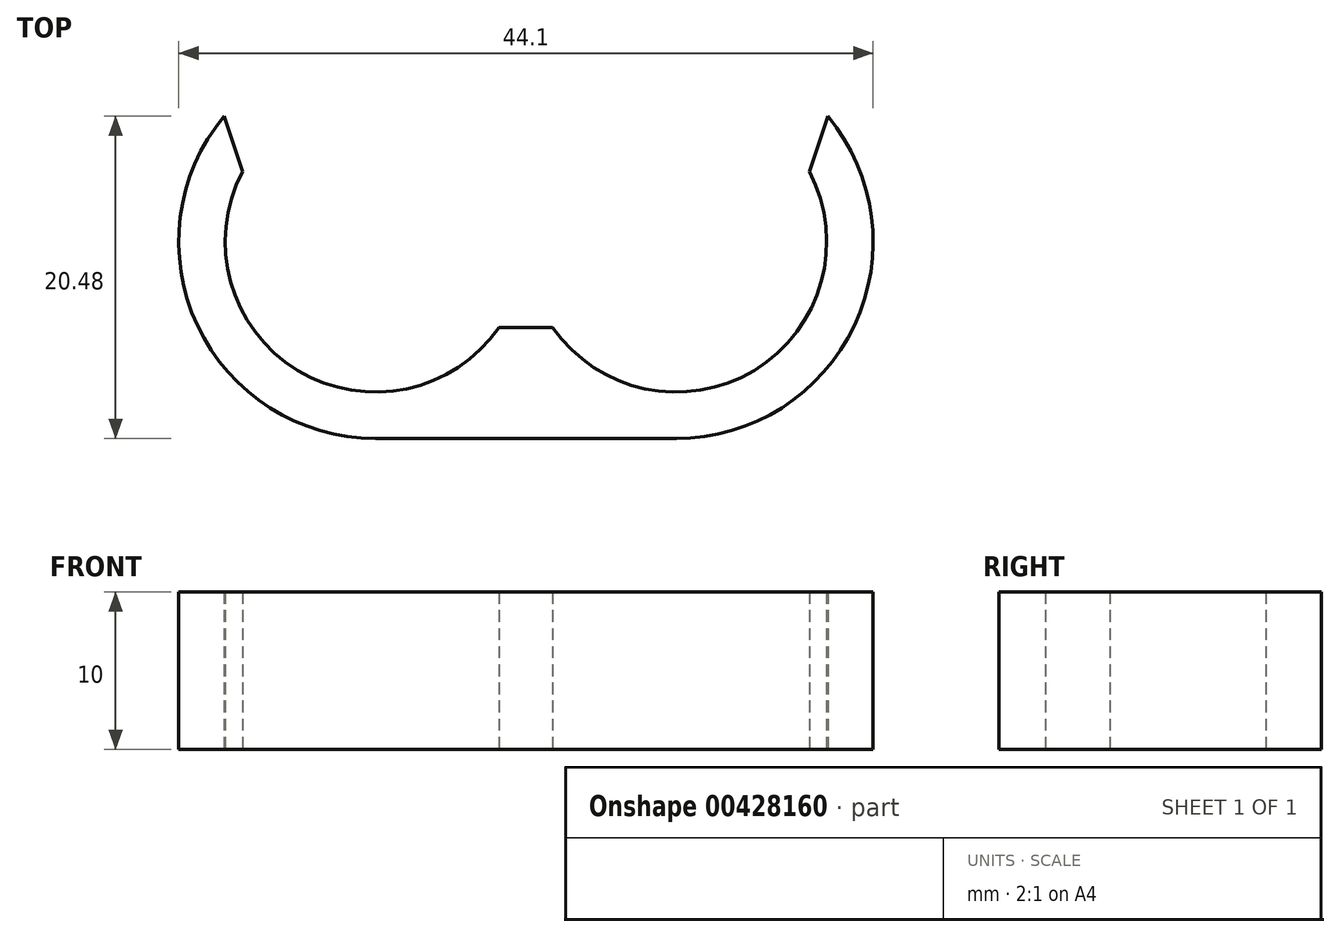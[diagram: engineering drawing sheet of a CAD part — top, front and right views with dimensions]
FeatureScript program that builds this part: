
annotation { "Feature Type Name" : "Feature", "Feature Type Description" : "" }
export const myFeature = defineFeature(function(context is Context, id is Id, definition is map)
    precondition{}
    {
        {
            var Q0;
            Q0=qCreatedBy(makeId("Top.planeOp"),FACE);
            var sketch = newSketch(context, id + "F0", { "sketchPlane" : qUnion([Q0])});
            skArc(sketch, "E0", {"start": v(-52.31, 34.5) * mm, "mid": v(-48.82, 21.88) * mm, "end": v(-36.01, 24.6) * mm});
            skArc(sketch, "E1", {"start": v(-32.6, 24.6) * mm, "mid": v(-19.8, 21.88) * mm, "end": v(-16.31, 34.5) * mm});
            skArc(sketch, "E2", {"start": v(-24.76, 17.55) * mm, "mid": v(-13.45, 24.73) * mm, "end": v(-15.14, 38.03) * mm});
            skLineSegment(sketch, "E3", {"start": v(-43.86, 17.55) * mm, "end": v(-24.76, 17.55) * mm});
            skLineSegment(sketch, "E4", {"start": v(-36.01, 24.6) * mm, "end": v(-32.6, 24.6) * mm});
            skArc(sketch, "E5.trimOffspring", {"start": v(-53.48, 38.03) * mm, "mid": v(-55.17, 24.73) * mm, "end": v(-43.86, 17.55) * mm});
            skLineSegment(sketch, "E6", {"start": v(-52.31, 34.5) * mm, "end": v(-53.48, 38.03) * mm});
            skLineSegment(sketch, "E7", {"start": v(-16.31, 34.5) * mm, "end": v(-15.14, 38.03) * mm});
            skSolve(sketch);
        }
        {
            var Q0;
            Q0=makeQuery(id+"F0.imprint","IMPRINT",FACE,{"disambiguationData":[TD([[makeQuery(id+"F0.imprint","IMPRINT",EDGE,{"derivedFrom":sQuery(id+"F0.wireOp",EDGE,"E0")}),-1.0]])]});
            extrude(context, id + "F1", {"entities" : qUnion([Q0]), "depth" : 10 * mm});
        }
    });
